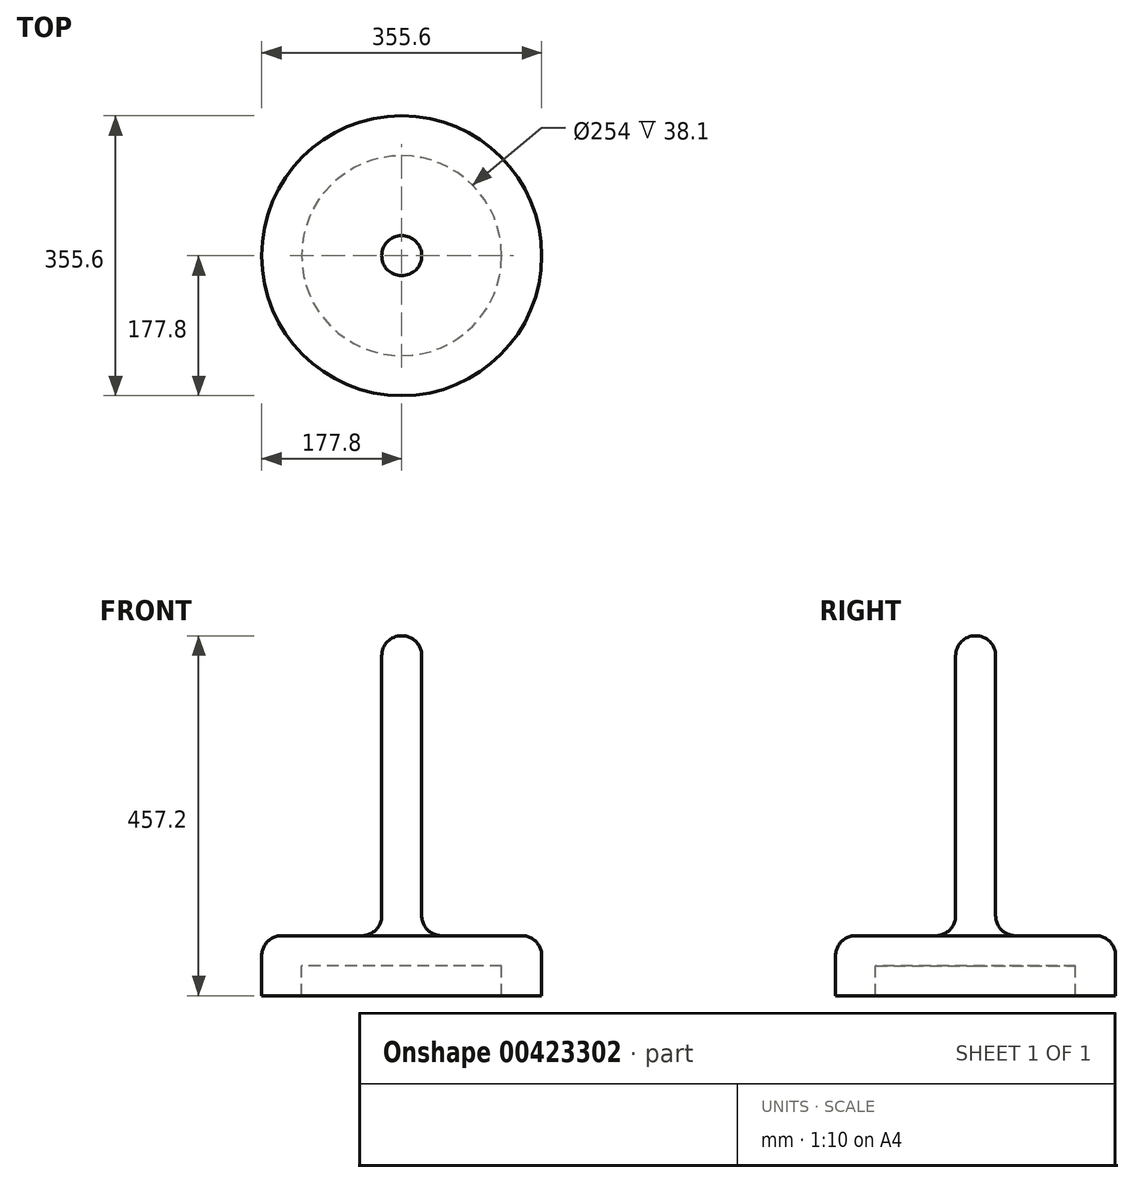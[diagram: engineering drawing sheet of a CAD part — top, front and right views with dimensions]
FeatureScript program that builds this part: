
annotation { "Feature Type Name" : "Feature", "Feature Type Description" : "" }
export const myFeature = defineFeature(function(context is Context, id is Id, definition is map)
    precondition{}
    {
        {
            var Q0;
            Q0=qCreatedBy(makeId("Front.planeOp"),FACE);
            var sketch = newSketch(context, id + "F0", { "sketchPlane" : qUnion([Q0])});
            skLineSegment(sketch, "E0", {"start": v(0, 0) * mm, "end": v(-127, 0) * mm});
            skLineSegment(sketch, "E1", {"start": v(-127, 0) * mm, "end": v(-127, -38.1) * mm});
            skLineSegment(sketch, "E2", {"start": v(-127, -38.1) * mm, "end": v(-177.8, -38.1) * mm});
            skLineSegment(sketch, "E3", {"start": v(-177.8, -38.1) * mm, "end": v(-177.8, 12.7) * mm});
            skLineSegment(sketch, "E4", {"start": v(-152.4, 38.1) * mm, "end": v(-50.8, 38.1) * mm});
            skLineSegment(sketch, "E5", {"start": v(-25.4, 63.5) * mm, "end": v(-25.4, 393.7) * mm});
            skLineSegment(sketch, "E6", {"start": v(0, 419.1) * mm, "end": v(0, 419.1) * mm});
            skLineSegment(sketch, "E7", {"start": v(0, 419.1) * mm, "end": v(0, 0) * mm});
            skPoint(sketch, "E8.visualSharp", {"position": v(-177.8, 38.1) * mm});
            skArc(sketch, "E8.filletArc", {"start": v(-152.4, 38.1) * mm, "mid": v(-170.36, 30.66) * mm, "end": v(-177.8, 12.7) * mm});
            skPoint(sketch, "E9.visualSharp", {"position": v(-25.4, 38.1) * mm});
            skArc(sketch, "E9.filletArc", {"start": v(-50.8, 38.1) * mm, "mid": v(-32.84, 45.54) * mm, "end": v(-25.4, 63.5) * mm});
            skPoint(sketch, "E10.visualSharp", {"position": v(-25.4, 419.1) * mm});
            skArc(sketch, "E10.filletArc", {"start": v(0, 419.1) * mm, "mid": v(-17.96, 411.66) * mm, "end": v(-25.4, 393.7) * mm});
            skSolve(sketch);
        }
        {
            var Q0;
            Q0=makeQuery(id+"F0.imprint","IMPRINT",FACE,{"disambiguationData":[TD([[makeQuery(id+"F0.imprint","IMPRINT",EDGE,{"derivedFrom":sQuery(id+"F0.wireOp",EDGE,"E0")}),-1.0]])]});
            var Q1;
            Q1=sQuery(id+"F0.wireOp",EDGE,"E7");
            revolve(context, id + "F1", {"entities" : qUnion([Q0]), "axis" : qUnion([Q1]), "revolveType" : RevolveType.FULL});
        }
    });
